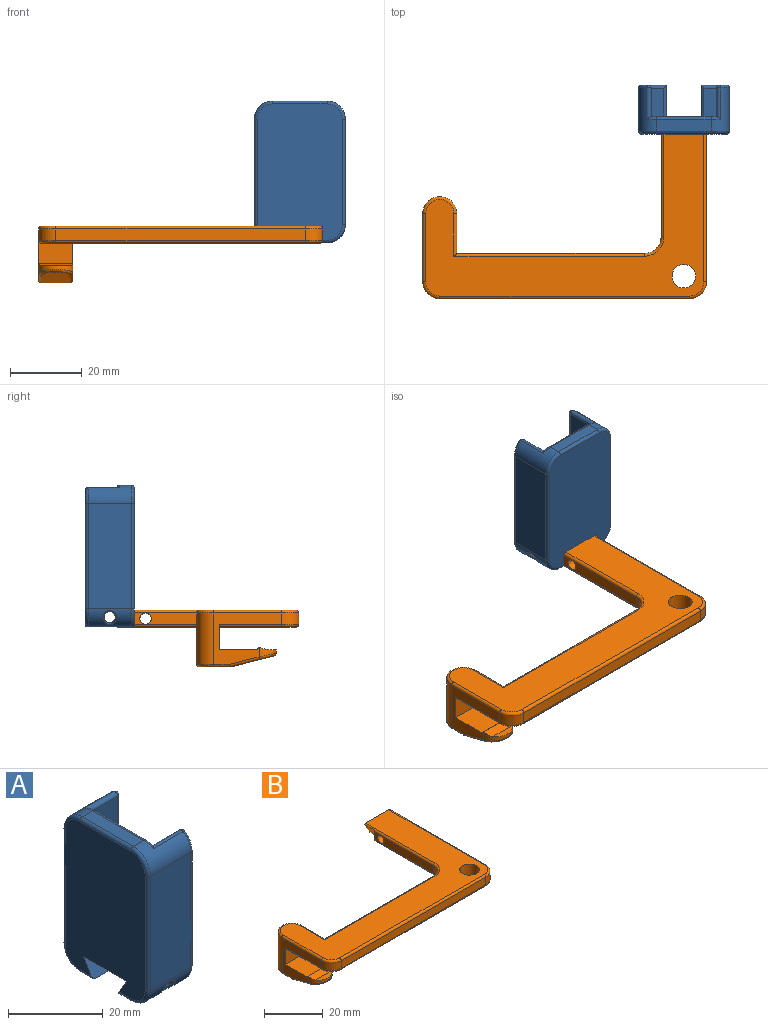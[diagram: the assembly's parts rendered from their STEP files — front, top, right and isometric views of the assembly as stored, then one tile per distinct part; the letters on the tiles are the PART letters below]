
ASSEMBLY  parts=2 mates=1
PART A: 72 faces, bbox 13.8x26.4x40.7 mm
  f0: plane 4.7x3.51mm, normal (1,0,0), area 6.5mm2, adj f3,f10,f20,f51
  f1: plane 34.19x18.47mm, normal (1,0,0), area 598.2mm2, adj f9,f13,f14,f15,f17,f18,f19,f26
  f2: plane 4.7x3.51mm, normal (1,0,0), area 6.5mm2, adj f6,f11,f12,f29
  f3: plane 12.07x3.93mm, normal (0,0,-1), area 19.1mm2, adj f0,f10,f23,f51,f56,f65
  f4: plane 38.1x23.81mm, normal (-1,0,0), area 850.3mm2, adj f9,f10,f11,f57,f58,f59,f60,f61
  f5: plane 29.53x12.07mm, normal (0,-1,0), area 356.2mm2, adj f22,f25,f35,f59
  f6: plane 12.07x3.93mm, normal (0,0,-1), area 19.1mm2, adj f2,f11,f22,f29,f31,f57
  f7: plane 29.53x12.07mm, normal (0,1,0), area 356.2mm2, adj f23,f24,f53,f63
  f8: plane 15.24x3.18mm, normal (0,0,1), area 48.4mm2, adj f24,f25,f42,f61
  f9: plane 12.86x12.8mm, normal (0,0,-1), area 73.6mm2, adj f1,f4,f10,f11,f12,f20,f26,f27
  f10: plane 4.96x4.89mm, normal (0,-0.87,0.5), area 25.7mm2, adj f0,f3,f4,f9,f65
  f11: plane 4.96x4.89mm, normal (0,0.87,0.5), area 25.7mm2, adj f2,f4,f6,f9,f57
  f12: plane 8.1x3.91mm, normal (0,1,0), area 20.6mm2, adj f2,f9,f28,f29,f69
  f13: plane 8.89x1.59mm, normal (0,1,0), area 14.1mm2, adj f1,f16,f26,f32
  f14: plane 8.1x3.52mm, normal (0,0,1), area 28.5mm2, adj f1,f15,f32,f34
  f15: plane 30.34x8.1mm, normal (0,1,0), area 245.6mm2, adj f1,f14,f36,f39
  f16: plane 37.42x7.08mm, normal (1,0,0), area 88.6mm2, adj f13,f27,f28,f31,f33,f34,f35,f36
  f17: plane 30.34x8.1mm, normal (0,-1,0), area 245.6mm2, adj f1,f18,f45,f46
  f18: plane 8.1x3.52mm, normal (0,0,1), area 28.5mm2, adj f1,f17,f41,f43
  f19: plane 8.89x1.59mm, normal (0,-1,0), area 14.1mm2, adj f1,f21,f41,f47
  f20: plane 8.1x3.91mm, normal (0,-1,0), area 20.6mm2, adj f0,f9,f51,f52,f70
  f21: plane 37.42x7.08mm, normal (1,0,0), area 88.6mm2, adj f19,f43,f45,f49,f50,f52,f53,f55
  f22: cylinder r=5.08mm len=12.07mm, axis (-1,0,0), area 82.1mm2, adj f5,f6,f33,f58,f71
  f23: cylinder r=5.08mm len=12.07mm, axis (1,0,0), area 82.1mm2, adj f3,f7,f55,f64,f68
  f24: cylinder r=5.08mm len=12.07mm, axis (-1,0,0), area 70.5mm2, adj f7,f8,f44,f46,f50,f62
  f25: cylinder r=5.08mm len=12.07mm, axis (1,0,0), area 70.5mm2, adj f5,f8,f37,f39,f40,f60
  f26: cylinder r=0.79mm len=8.89mm, axis (-1,0,0), area 10.6mm2, adj f1,f9,f13,f27
  f27: cylinder r=0.79mm len=2.37mm, axis (0,1,0), area 2mm2, adj f9,f16,f26,f28
  f28: cylinder r=0.79mm len=4.7mm, axis (0,0,-1), area 5.4mm2, adj f12,f16,f27,f30
  f29: cylinder r=0.79mm len=8.1mm, axis (1,0,0), area 10.1mm2, adj f2,f6,f12,f30
  f30: sphere r=0.79mm, area 0.6mm2, adj f28,f29,f31
  f31: cylinder r=0.79mm len=0.79mm, axis (0,-1,0), area 0.5mm2, adj f6,f16,f30,f33
  f32: cylinder r=0.79mm len=8.89mm, axis (-1,0,0), area 10.6mm2, adj f1,f13,f14,f34
  f33: torus R=4.29mm, axis (1,0,0), area 9.4mm2, adj f16,f22,f31,f35
  f34: cylinder r=0.79mm len=5.11mm, axis (0,1,0), area 5.4mm2, adj f14,f16,f32,f36
  f35: cylinder r=0.79mm len=29.53mm, axis (0,0,1), area 36.8mm2, adj f5,f16,f33,f37
  f36: cylinder r=0.79mm len=31.13mm, axis (0,0,-1), area 38.3mm2, adj f15,f16,f34,f38
  f37: torus R=4.29mm, axis (1,0,0), area 6mm2, adj f16,f25,f35,f38
  f38: sphere r=0.79mm, area 1.3mm2, adj f36,f37,f39
  f39: cylinder r=0.79mm len=8.89mm, axis (1,0,0), area 14.3mm2, adj f1,f15,f25,f38,f40
  f40: torus R=4.29mm, axis (1,0,0), area 2.9mm2, adj f1,f25,f39,f42
  f41: cylinder r=0.79mm len=8.89mm, axis (1,0,0), area 10.6mm2, adj f1,f18,f19,f43
  f42: cylinder r=0.79mm len=15.24mm, axis (0,1,0), area 19mm2, adj f1,f8,f40,f44
  f43: cylinder r=0.79mm len=5.11mm, axis (0,1,0), area 5.4mm2, adj f18,f21,f41,f45
  f44: torus R=4.29mm, axis (1,0,0), area 2.9mm2, adj f1,f24,f42,f46
  f45: cylinder r=0.79mm len=31.13mm, axis (0,0,1), area 38.3mm2, adj f17,f21,f43,f48
  f46: cylinder r=0.79mm len=8.89mm, axis (-1,0,0), area 14.3mm2, adj f1,f17,f24,f44,f48
  f47: cylinder r=0.79mm len=8.89mm, axis (1,0,0), area 10.6mm2, adj f1,f9,f19,f49
  f48: sphere r=0.79mm, area 1.5mm2, adj f45,f46,f50
  f49: cylinder r=0.79mm len=2.37mm, axis (0,1,0), area 2mm2, adj f9,f21,f47,f52
  f50: torus R=4.29mm, axis (1,0,0), area 6mm2, adj f21,f24,f48,f53
  f51: cylinder r=0.79mm len=8.1mm, axis (-1,0,0), area 10.1mm2, adj f0,f3,f20,f54
  f52: cylinder r=0.79mm len=4.7mm, axis (0,0,1), area 5.4mm2, adj f20,f21,f49,f54
  f53: cylinder r=0.79mm len=29.53mm, axis (0,0,-1), area 36.8mm2, adj f7,f21,f50,f55
  f54: sphere r=0.79mm, area 1mm2, adj f51,f52,f56
  f55: torus R=4.29mm, axis (1,0,0), area 9.4mm2, adj f21,f23,f53,f56
  f56: cylinder r=0.79mm len=0.79mm, axis (0,-1,0), area 0.5mm2, adj f3,f21,f54,f55
  f57: cylinder r=0.79mm len=3.93mm, axis (0,1,0), area 4.6mm2, adj f4,f6,f11,f58
  f58: torus R=4.29mm, axis (1,0,0), area 9.4mm2, adj f4,f22,f57,f59
  f59: cylinder r=0.79mm len=29.53mm, axis (0,0,-1), area 36.8mm2, adj f4,f5,f58,f60
  f60: torus R=4.29mm, axis (1,0,0), area 9.4mm2, adj f4,f25,f59,f61
  f61: cylinder r=0.79mm len=15.24mm, axis (0,-1,0), area 19mm2, adj f4,f8,f60,f62
  f62: torus R=4.29mm, axis (1,0,0), area 9.4mm2, adj f4,f24,f61,f63
  f63: cylinder r=0.79mm len=29.53mm, axis (0,0,1), area 36.8mm2, adj f4,f7,f62,f64
  f64: torus R=4.29mm, axis (1,0,0), area 9.4mm2, adj f4,f23,f63,f65
  f65: cylinder r=0.79mm len=3.93mm, axis (0,1,0), area 4.6mm2, adj f3,f4,f10,f64
  f66: cylinder r=1.59mm len=5.71mm, axis (0,-1,0), area 48.1mm2, adj f68,f70
  f67: cylinder r=1.59mm len=5.71mm, axis (0,-1,0), area 48.1mm2, adj f69,f71
  f68: bspline ~3.96x3.83mm, area 5.5mm2, adj f23,f66
  f69: cone r=1.59mm half-angle=45deg, axis (0,1,0), area 4.3mm2, adj f12,f67
  f70: cone r=1.87mm half-angle=45deg, axis (0,-1,0), area 4.3mm2, adj f20,f66
  f71: bspline ~3.96x3.83mm, area 5.5mm2, adj f22,f67
PART B: 57 faces, bbox 80.2x51.2x15.9 mm
  f0: plane 3.18x3.18mm, normal (-1,0,0), area 6.1mm2, adj f25,f28,f33,f47
  f1: plane 38.1x3.18mm, normal (1,0,0), area 117mm2, adj f23,f28,f29,f43
  f2: plane 77.79x50.01mm, normal (0,0,-1), area 1325.5mm2, adj f3,f9,f14,f24,f25,f26,f27,f39
  f3: plane 12.35x4.76mm, normal (0,1,0), area 47.2mm2, adj f2,f11,f24,f26,f29,f33
  f4: plane 3.18x3.18mm, normal (1,0,0), area 6.1mm2, adj f27,f28,f29,f43
  f5: plane 25.4x3.18mm, normal (-1,0,0), area 76.7mm2, adj f20,f28,f33,f47
  f6: plane 52.39x3.18mm, normal (0,1,0), area 166.3mm2, adj f7,f20,f37,f45
  f7: plane 14.29x12.7mm, normal (1,0,0), area 89.2mm2, adj f6,f13,f14,f16,f17,f19,f21,f38
  f8: plane 19.05x14.29mm, normal (-1,0,0), area 114.4mm2, adj f13,f14,f16,f17,f19,f21,f22,f34
  f9: cylinder r=3.3mm len=6.6mm, axis (0,0,-1), area 98.8mm2, adj f2,f11
  f10: plane 69.85x3.18mm, normal (0,-1,0), area 221.8mm2, adj f22,f23,f31,f41
  f11: plane 77.79x50.01mm, normal (0,0,1), area 1381.5mm2, adj f3,f9,f29,f30,f31,f32,f33,f34
  f12: plane 7.8x2.03mm, normal (0,0,1), area 11.1mm2, adj f17,f19
  f13: plane 10.67x9.53mm, normal (0,0,1), area 101.6mm2, adj f7,f8,f14,f16
  f14: plane 9.53x7.14mm, normal (0,-1,0), area 60.8mm2, adj f2,f7,f8,f13,f39,f44
  f15: plane 8.63x7.94mm, normal (0,0,-1), area 61.8mm2, adj f50,f54,f55,f56
  f16: cylinder r=0.79mm len=9.53mm, axis (-1,0,0), area 8mm2, adj f7,f8,f13,f17
  f17: plane 9.53x2.77mm, normal (0,-0.24,0.97), area 25.6mm2, adj f7,f8,f12,f16,f19
  f18: plane 12x7.94mm, normal (0,-0.24,-0.97), area 91.2mm2, adj f48,f49,f50,f51
  f19: cylinder r=4.76mm len=9.53mm, axis (0,0,1), area 21.8mm2, adj f7,f8,f12,f17,f48
  f20: cylinder r=4.76mm len=4.76mm, axis (0,0,-1), area 23.8mm2, adj f5,f6,f35,f46
  f21: cylinder r=4.76mm len=14.29mm, axis (0,0,-1), area 213.8mm2, adj f7,f8,f36,f56
  f22: cylinder r=4.76mm len=4.76mm, axis (0,0,-1), area 23.8mm2, adj f8,f10,f32,f40
  f23: cylinder r=4.76mm len=4.76mm, axis (0,0,-1), area 23.8mm2, adj f1,f10,f30,f42
  f24: plane 4.76x4.46mm, normal (-0.87,0,-0.5), area 24.5mm2, adj f2,f3,f25,f33
  f25: plane 4.46x2.75mm, normal (0,1,0), area 6.4mm2, adj f0,f2,f24,f33,f47
  f26: plane 4.76x4.46mm, normal (0.87,0,-0.5), area 24.5mm2, adj f2,f3,f27,f29
  f27: plane 4.46x2.75mm, normal (0,1,0), area 6.4mm2, adj f2,f4,f26,f29,f43
  f28: cylinder r=1.59mm len=12.7mm, axis (1,0,0), area 126.7mm2, adj f0,f1,f4,f5
  f29: cylinder r=0.79mm len=46.04mm, axis (0,-1,0), area 54.9mm2, adj f1,f3,f4,f11,f26,f27,f30
  f30: torus R=3.97mm, axis (0,0,1), area 8.8mm2, adj f11,f23,f29,f31
  f31: cylinder r=0.79mm len=69.85mm, axis (-1,0,0), area 87.1mm2, adj f10,f11,f30,f32
  f32: torus R=3.97mm, axis (0,0,1), area 8.8mm2, adj f11,f22,f31,f34
  f33: cylinder r=0.79mm len=33.34mm, axis (0,1,0), area 39mm2, adj f0,f3,f5,f11,f24,f25,f35
  f34: cylinder r=0.79mm len=19.05mm, axis (0,1,0), area 23.8mm2, adj f8,f11,f32,f36
  f35: torus R=5.56mm, axis (0,0,1), area 9.9mm2, adj f11,f20,f33,f37
  f36: torus R=3.97mm, axis (0,0,1), area 17.5mm2, adj f11,f21,f34,f38
  f37: cylinder r=0.79mm len=53.18mm, axis (1,0,0), area 65.7mm2, adj f6,f11,f35,f38
  f38: cylinder r=0.79mm len=11.91mm, axis (0,-1,0), area 14.2mm2, adj f7,f11,f36,f37
  f39: cylinder r=0.79mm len=17.46mm, axis (0,-1,0), area 21.8mm2, adj f2,f8,f14,f40
  f40: torus R=3.97mm, axis (0,0,1), area 8.8mm2, adj f2,f22,f39,f41
  f41: cylinder r=0.79mm len=69.85mm, axis (1,0,0), area 87.1mm2, adj f2,f10,f40,f42
  f42: torus R=3.97mm, axis (0,0,1), area 8.8mm2, adj f2,f23,f41,f43
  f43: cylinder r=0.79mm len=41.28mm, axis (0,1,0), area 51.5mm2, adj f1,f2,f4,f27,f42
  f44: cylinder r=0.79mm len=10.32mm, axis (0,1,0), area 12.2mm2, adj f2,f7,f14,f45
  f45: cylinder r=0.79mm len=53.18mm, axis (-1,0,0), area 65.7mm2, adj f2,f6,f44,f46
  f46: torus R=5.56mm, axis (0,0,1), area 9.9mm2, adj f2,f20,f45,f47
  f47: cylinder r=0.79mm len=28.58mm, axis (0,-1,0), area 35.6mm2, adj f0,f2,f5,f25,f46
  f48: bspline ~9.53x4.76mm, area 15.9mm2, adj f18,f19,f49,f51
  f49: cylinder r=0.79mm len=8.23mm, axis (0,0.97,-0.24), area 10.3mm2, adj f8,f18,f48,f52
  f50: cylinder r=0.79mm len=7.94mm, axis (1,0,0), area 1.5mm2, adj f15,f18,f52,f53
  f51: cylinder r=0.79mm len=8.23mm, axis (0,-0.97,0.24), area 10.3mm2, adj f7,f18,f48,f53
  f52: sphere r=0.79mm, area 0.2mm2, adj f49,f50,f54
  f53: sphere r=0.79mm, area 0.2mm2, adj f50,f51,f55
  f54: cylinder r=0.79mm len=4.66mm, axis (0,-1,0), area 5.8mm2, adj f8,f15,f52,f56
  f55: cylinder r=0.79mm len=4.66mm, axis (0,-1,0), area 5.8mm2, adj f7,f15,f53,f56
  f56: torus R=3.97mm, axis (0,0,-1), area 17.5mm2, adj f15,f21,f54,f55
PLACE A rot(axis=(0,0,1),90deg) t=(52.68,31.72,-1.11)mm
PLACE B rot(axis=(0,0,1),0deg) t=(-20.34,14.22,-21.01)mm
MATE slider B.f3 <-> A.f4  axis (0,1,0) through (52.68,36.44,-16.25)mm
